# Revit family: HVAC_Mechanical-Ventilation_Envira-North_Jazz_Gearless-Ceiling-Fan-w-Light2
name_source: partatom
category: Electrical Fixtures
units: mm (PartAtom-declared; Revit-internal decimal feet)

## family parameters
Always vertical = No
Cut with Voids When Loaded = No
Maintain Annotation Orientation = No
OmniClass Number = 23.75.35.17.17.11
OmniClass Title = Ceiling Fans
Part Type = Normal
Room Calculation Point = No
Round Connector Dimension = Use Diameter
Shared = No
Work Plane-Based = Yes

## types (1)
- Default - please load Revit Family Type Catalog
    Alternate Voltage = 240 V
    Blades Material = Envira North Systems - Blade Paint - Slate Gray
    CFEI 40% Speed = 0 ft³·h/(min·Btu)
    CFEI High Speed = 0 ft³·h/(min·Btu)
    Date Updated = 17/12/2024
    Default Elevation = 0.00"
    Description = Jazz Fan
    Design Ventilation Air Flow = 27000 CFM
    Diameter = 84.00"
    Manufacturer = Envira-North Systems
    Maximum Effective Diameter = 582.00"
    Maximum Velocity = 0 FPM
    Model = EN570X5007
    Number of Poles = 3
    Power Factor = 1
    Product Material = Envira North Systems - Metal
    Product Page URL = https://www.enviranorth.com
    Sound Rating = 39
    URL = https://www.enviranorth.com
    Version = 1
    Voltage = 120 V
    Wattage = 264 W
    Weight = 70.00 lbf
    z_Blade Length = Blade : 7FT
    z_Clearance Blades = 12.00"
    z_Clearance Blades Diameter = 100.00"
    z_Clearance to Floor = 144.00"
    z_Radius = 42.00"

## geometry (parser evidence)
native form markers: Sweep x6
no freeform markers — native parametric forms only
